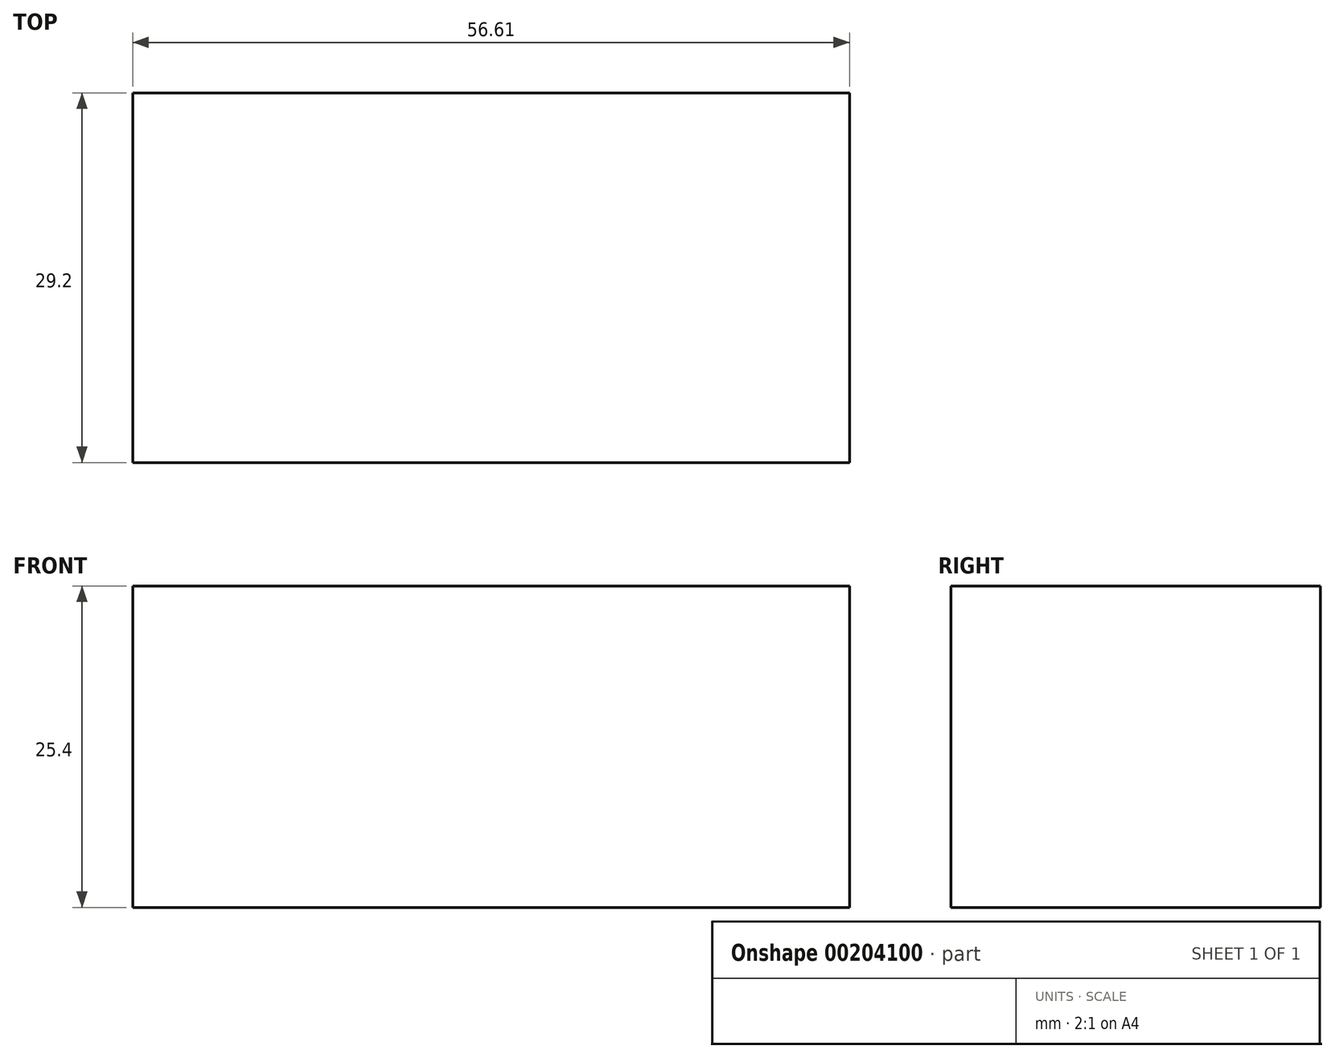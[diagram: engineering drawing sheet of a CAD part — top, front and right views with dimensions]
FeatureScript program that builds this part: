
annotation { "Feature Type Name" : "Feature", "Feature Type Description" : "" }
export const myFeature = defineFeature(function(context is Context, id is Id, definition is map)
    precondition{}
    {
        {
            var Q0;
            Q0=qCreatedBy(makeId("Top.planeOp"),FACE);
            var sketch = newSketch(context, id + "F0", { "sketchPlane" : qUnion([Q0])});
            skLineSegment(sketch, "E0.bottom", {"start": v(0, 0) * mm, "end": v(56.61, 0) * mm});
            skLineSegment(sketch, "E0.top", {"start": v(0, 29.2) * mm, "end": v(56.61, 29.2) * mm});
            skLineSegment(sketch, "E0.left", {"start": v(0, 0) * mm, "end": v(0, 29.2) * mm});
            skLineSegment(sketch, "E0.right", {"start": v(56.61, 0) * mm, "end": v(56.61, 29.2) * mm});
            skSolve(sketch);
        }
        {
            var Q0;
            Q0=makeQuery(id+"F0.imprint","IMPRINT",FACE,{"disambiguationData":[TD([[makeQuery(id+"F0.imprint","IMPRINT",EDGE,{"derivedFrom":sQuery(id+"F0.wireOp",EDGE,"E0.bottom")}),1.0]])]});
            extrude(context, id + "F1", {"entities" : qUnion([Q0]), "depth" : 25.4 * mm});
        }
    });
